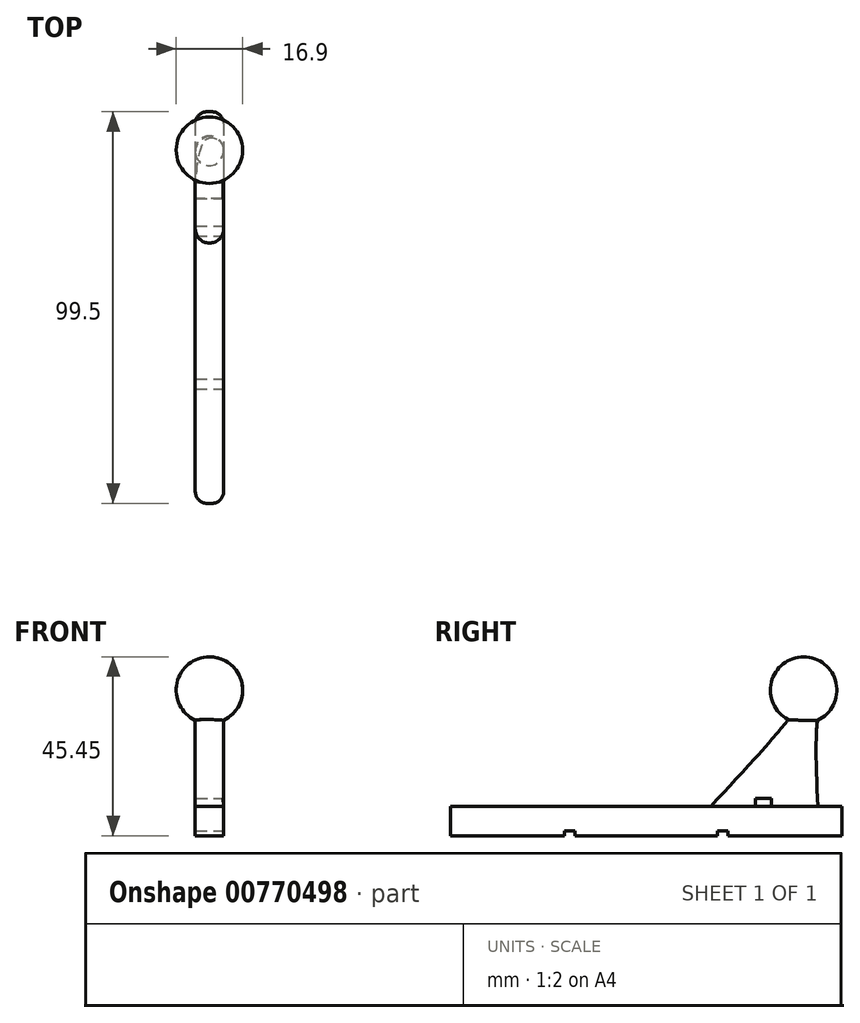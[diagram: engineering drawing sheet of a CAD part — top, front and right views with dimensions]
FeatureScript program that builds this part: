
annotation { "Feature Type Name" : "Feature", "Feature Type Description" : "" }
export const myFeature = defineFeature(function(context is Context, id is Id, definition is map)
    precondition{}
    {
        {
            var Q0;
            Q0=qCreatedBy(makeId("Top.planeOp"),FACE);
            var sketch = newSketch(context, id + "F0", { "sketchPlane" : qUnion([Q0])});
            skLineSegment(sketch, "E0.bottom", {"start": v(0.6, 49.75) * mm, "end": v(-0.6, 49.75) * mm});
            skLineSegment(sketch, "E0.top", {"start": v(0.6, -49.75) * mm, "end": v(-0.6, -49.75) * mm});
            skLineSegment(sketch, "E0.left", {"start": v(3.6, 46.75) * mm, "end": v(3.6, -46.75) * mm});
            skLineSegment(sketch, "E0.right", {"start": v(-3.6, 46.75) * mm, "end": v(-3.6, -46.75) * mm});
            skPoint(sketch, "E0.middle", {"position": v(0, 0) * mm});
            skPoint(sketch, "E1.visualSharp", {"position": v(3.6, 49.75) * mm});
            skArc(sketch, "E1.filletArc", {"start": v(3.6, 46.75) * mm, "mid": v(2.72, 48.87) * mm, "end": v(0.6, 49.75) * mm});
            skPoint(sketch, "E2.visualSharp", {"position": v(-3.6, 49.75) * mm});
            skArc(sketch, "E2.filletArc", {"start": v(-0.6, 49.75) * mm, "mid": v(-2.72, 48.87) * mm, "end": v(-3.6, 46.75) * mm});
            skPoint(sketch, "E3.visualSharp", {"position": v(3.6, -49.75) * mm});
            skArc(sketch, "E3.filletArc", {"start": v(0.6, -49.75) * mm, "mid": v(2.72, -48.87) * mm, "end": v(3.6, -46.75) * mm});
            skPoint(sketch, "E4.visualSharp", {"position": v(-3.6, -49.75) * mm});
            skArc(sketch, "E4.filletArc", {"start": v(-3.6, -46.75) * mm, "mid": v(-2.72, -48.87) * mm, "end": v(-0.6, -49.75) * mm});
            skSolve(sketch);
        }
        {
            var Q0;
            Q0=makeQuery(id+"F0.imprint","IMPRINT",FACE,{"disambiguationData":[TD([[makeQuery(id+"F0.imprint","IMPRINT",EDGE,{"derivedFrom":sQuery(id+"F0.wireOp",EDGE,"E0.bottom")}),1.0]])]});
            extrude(context, id + "F1", {"entities" : qUnion([Q0]), "depth" : 7.5 * mm, "offsetDistance" : 25 * mm});
        }
        {
            var Q0;
            Q0=makeQuery(id+"F1.opExtrude","CAP_FACE",FACE,{"disambiguationData":[OSD([sQuery(id+"F0.wireOp",EDGE,"E0.bottom"),sQuery(id+"F0.wireOp",EDGE,"E0.top"),sQuery(id+"F0.wireOp",EDGE,"E0.left"),sQuery(id+"F0.wireOp",EDGE,"E0.right"),sQuery(id+"F0.wireOp",EDGE,"E1.filletArc"),sQuery(id+"F0.wireOp",EDGE,"E2.filletArc"),sQuery(id+"F0.wireOp",EDGE,"E3.filletArc"),sQuery(id+"F0.wireOp",EDGE,"E4.filletArc")])],"isStart":true});
            var sketch = newSketch(context, id + "F2", { "sketchPlane" : qUnion([Q0])});
            skLineSegment(sketch, "E5.bottom", {"start": v(-3.6, 20.75) * mm, "end": v(3.6, 20.75) * mm});
            skLineSegment(sketch, "E5.top", {"start": v(-3.6, 18.15) * mm, "end": v(3.6, 18.15) * mm});
            skLineSegment(sketch, "E5.left", {"start": v(-3.6, 20.75) * mm, "end": v(-3.6, 18.15) * mm});
            skLineSegment(sketch, "E5.right", {"start": v(3.6, 20.75) * mm, "end": v(3.6, 18.15) * mm});
            skLineSegment(sketch, "E6.bottom", {"start": v(-3.6, -18.15) * mm, "end": v(3.6, -18.15) * mm});
            skLineSegment(sketch, "E6.top", {"start": v(-3.6, -20.75) * mm, "end": v(3.6, -20.75) * mm});
            skLineSegment(sketch, "E6.left", {"start": v(-3.6, -18.15) * mm, "end": v(-3.6, -20.75) * mm});
            skLineSegment(sketch, "E6.right", {"start": v(3.6, -18.15) * mm, "end": v(3.6, -20.75) * mm});
            skSolve(sketch);
        }
        {
            var Q0;
            Q0=qCreatedBy(makeId("Top.planeOp"),FACE);
            cPlane(context, id + "F3", {"entities" : qUnion([Q0]), "cplaneType" : CPlaneType.OFFSET, "offset" : 30 * mm, "width" : 150 * mm, "height" : 150 * mm});
        }
        {
            var Q0;
            Q0=qSketchRegion(id+"F2",true);
            extrude(context, id + "F4", {"entities" : qUnion([Q0]), "operationType" : NewBodyOperationType.REMOVE, "oppositeDirection" : true, "depth" : 1.2 * mm, "offsetDistance" : 25 * mm});
        }
        {
            var Q0;
            Q0=makeQuery(id+"F1.opExtrude","CAP_FACE",FACE,{"disambiguationData":[OSD([sQuery(id+"F0.wireOp",EDGE,"E0.bottom"),sQuery(id+"F0.wireOp",EDGE,"E0.top"),sQuery(id+"F0.wireOp",EDGE,"E0.left"),sQuery(id+"F0.wireOp",EDGE,"E0.right"),sQuery(id+"F0.wireOp",EDGE,"E1.filletArc"),sQuery(id+"F0.wireOp",EDGE,"E2.filletArc"),sQuery(id+"F0.wireOp",EDGE,"E3.filletArc"),sQuery(id+"F0.wireOp",EDGE,"E4.filletArc")])],"isStart":false});
            var sketch = newSketch(context, id + "F5", { "sketchPlane" : qUnion([Q0])});
            skArc(sketch, "E7", {"start": v(3.6, 40) * mm, "mid": v(0, 43.6) * mm, "end": v(-3.6, 40) * mm});
            skArc(sketch, "E8", {"start": v(-3.6, 20) * mm, "mid": v(0, 16.4) * mm, "end": v(3.6, 20) * mm});
            skLineSegment(sketch, "E9", {"start": v(-3.6, 40) * mm, "end": v(-3.6, 20) * mm});
            skLineSegment(sketch, "E10", {"start": v(3.6, 20) * mm, "end": v(3.6, 40) * mm});
            skSolve(sketch);
        }
        {
            var Q0;
            Q0=qCreatedBy(makeId("Front.planeOp"),FACE);
            cPlane(context, id + "F6", {"entities" : qUnion([Q0]), "cplaneType" : CPlaneType.OFFSET, "offset" : 40 * mm, "oppositeDirection" : true, "width" : 150 * mm, "height" : 150 * mm});
        }
        {
            var Q0;
            Q0=qCreatedBy(id+"F3.planeOp",FACE);
            var sketch = newSketch(context, id + "F7", { "sketchPlane" : qUnion([Q0])});
            skCircle(sketch, "E11", {"center": v(0, 40) * mm, "radius": 3.6 * mm});
            skSolve(sketch);
        }
        {
            var Q0;
            Q0=qCreatedBy(id+"F6.planeOp",FACE);
            var sketch = newSketch(context, id + "F8", { "sketchPlane" : qUnion([Q0])});
            skArc(sketch, "E12", {"start": v(0, 45.45) * mm, "mid": v(-8.45, 37) * mm, "end": v(0, 28.55) * mm});
            skLineSegment(sketch, "E13", {"start": v(0, 28.55) * mm, "end": v(0, 45.45) * mm});
            skPoint(sketch, "E14.orphan", {"position": v(0, 27.71) * mm});
            skSolve(sketch);
        }
        {
            var Q0;
            Q0=qSketchRegion(id+"F8",true);
            var Q1;
            Q1=sQuery(id+"F8.wireOp",EDGE,"E13");
            revolve(context, id + "F9", {"operationType" : NewBodyOperationType.ADD, "surfaceOperationType" : NewSurfaceOperationType.NEW, "entities" : qUnion([Q0]), "axis" : qUnion([Q1]), "revolveType" : RevolveType.FULL});
        }
        {
            var Q1;
            Q1=qSketchRegion(id+"F7",true);
            var Q2;
            Q2=qSketchRegion(id+"F5",true);
            loft(context, id + "F10", {"operationType" : NewBodyOperationType.ADD, "sheetProfilesArray" : [{ "sheetProfileEntities" : qUnion([Q1]) }, { "sheetProfileEntities" : qUnion([Q2]) }]});
        }
        {
            var Q0;
            Q0=makeQuery(id+"F1.opExtrude","SWEPT_FACE",FACE,{"disambiguationData":[OSD([sQuery(id+"F0.wireOp",EDGE,"E0.left")])]});
            var sketch = newSketch(context, id + "F11", { "sketchPlane" : qUnion([Q0])});
            skLineSegment(sketch, "E15.bottom", {"start": v(27.75, 7.5) * mm, "end": v(31.75, 7.5) * mm});
            skLineSegment(sketch, "E15.top", {"start": v(27.75, 9.5) * mm, "end": v(31.75, 9.5) * mm});
            skLineSegment(sketch, "E15.left", {"start": v(27.75, 7.5) * mm, "end": v(27.75, 9.5) * mm});
            skLineSegment(sketch, "E15.right", {"start": v(31.75, 7.5) * mm, "end": v(31.75, 9.5) * mm});
            skSolve(sketch);
        }
        {
            var Q0;
            Q0=qSketchRegion(id+"F11",true);
            extrude(context, id + "F12", {"entities" : qUnion([Q0]), "operationType" : NewBodyOperationType.REMOVE, "oppositeDirection" : true, "depth" : 25 * mm, "offsetDistance" : 25 * mm});
        }
    });
